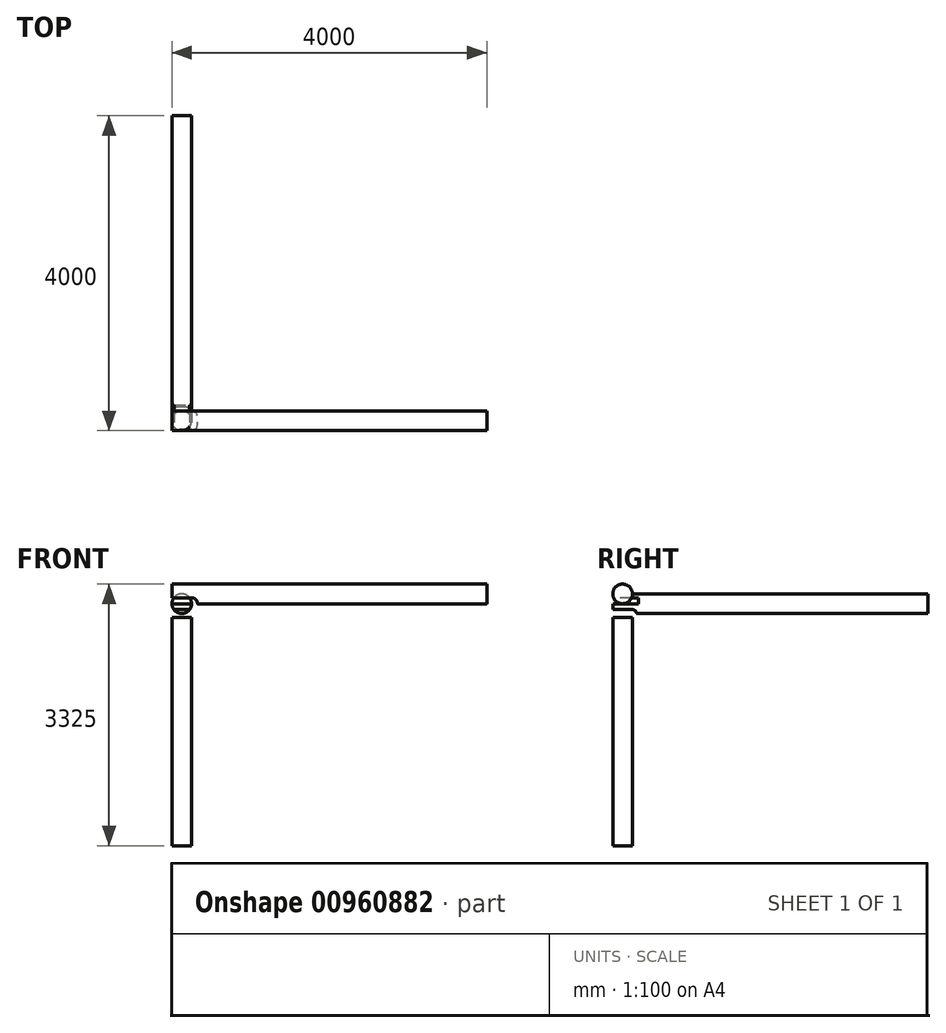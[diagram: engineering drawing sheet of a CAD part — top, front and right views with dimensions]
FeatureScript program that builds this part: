
annotation { "Feature Type Name" : "Feature", "Feature Type Description" : "" }
export const myFeature = defineFeature(function(context is Context, id is Id, definition is map)
    precondition{}
    {
        {
            var Q0;
            Q0=qCreatedBy(makeId("Top.planeOp"),FACE);
            var sketch = newSketch(context, id + "F0", { "sketchPlane" : qUnion([Q0])});
            skCircle(sketch, "E0", {"center": v(0, 0) * mm, "radius": 125 * mm});
            skSolve(sketch);
        }
        {
            var Q0;
            Q0=makeQuery(id+"F0.imprint","IMPRINT",FACE,{"disambiguationData":[TD([[makeQuery(id+"F0.imprint","IMPRINT",EDGE,{"derivedFrom":sQuery(id+"F0.wireOp",EDGE,"E0")}),1.0]])]});
            extrude(context, id + "F1", {"entities" : qUnion([Q0]), "oppositeDirection" : true, "depth" : 3000 * mm, "offsetDistance" : 25 * mm});
        }
        {
            var Q0;
            Q0=qCreatedBy(makeId("Front.planeOp"),FACE);
            cPlane(context, id + "F2", {"entities" : qUnion([Q0]), "cplaneType" : CPlaneType.OFFSET, "offset" : 125 * mm, "width" : 150 * mm, "height" : 150 * mm});
        }
        {
            var Q0;
            Q0=qCreatedBy(id+"F2.planeOp",FACE);
            var sketch = newSketch(context, id + "F3", { "sketchPlane" : qUnion([Q0])});
            skCircle(sketch, "E1", {"center": v(0, 75) * mm, "radius": 125 * mm});
            skSolve(sketch);
        }
        {
            var Q0;
            Q0=makeQuery(id+"F3.imprint","IMPRINT",FACE,{"disambiguationData":[TD([[makeQuery(id+"F3.imprint","IMPRINT",EDGE,{"derivedFrom":sQuery(id+"F3.wireOp",EDGE,"E1")}),1.0]])]});
            extrude(context, id + "F4", {"entities" : qUnion([Q0]), "oppositeDirection" : true, "depth" : 4000 * mm, "offsetDistance" : 25 * mm});
        }
        {
            var Q0;
            Q0=qCreatedBy(makeId("Right.planeOp"),FACE);
            var sketch = newSketch(context, id + "F5", { "sketchPlane" : qUnion([Q0])});
            skLineSegment(sketch, "E2", {"start": v(3875, -50) * mm, "end": v(-125, -50) * mm, "construction": true});
            skLineSegment(sketch, "E3", {"start": v(125, 0) * mm, "end": v(125, -3000) * mm, "construction": true});
            skLineSegment(sketch, "E4.0", {"start": v(-125, -50) * mm, "end": v(-125, 200) * mm, "construction": true});
            skLineSegment(sketch, "E5", {"start": v(125, 0) * mm, "end": v(-125, 0) * mm});
            skLineSegment(sketch, "E6", {"start": v(-125, 0) * mm, "end": v(-125, 150) * mm});
            skLineSegment(sketch, "E7", {"start": v(-125, 150) * mm, "end": v(125, 150) * mm});
            skLineSegment(sketch, "E8", {"start": v(125, 150) * mm, "end": v(125, 250) * mm});
            skLineSegment(sketch, "E9", {"start": v(125, 250) * mm, "end": v(-212.51, 250) * mm});
            skLineSegment(sketch, "E10", {"start": v(-212.51, 250) * mm, "end": v(-212.51, -100) * mm});
            skLineSegment(sketch, "E11", {"start": v(-212.51, -100) * mm, "end": v(216.52, -100) * mm});
            skLineSegment(sketch, "E12", {"start": v(216.52, -100) * mm, "end": v(216.52, -50) * mm});
            skLineSegment(sketch, "E13", {"start": v(-125, 200) * mm, "end": v(3875, 200) * mm, "construction": true});
            skArc(sketch, "E14", {"start": v(125, 0) * mm, "mid": v(160.36, -14.64) * mm, "end": v(175, -50) * mm});
            skLineSegment(sketch, "E15", {"start": v(175, -50) * mm, "end": v(216.52, -50) * mm});
            skSolve(sketch);
        }
        {
            var Q0;
            Q0=makeQuery(id+"F5.imprint","IMPRINT",FACE,{"disambiguationData":[TD([[makeQuery(id+"F5.imprint","IMPRINT",EDGE,{"derivedFrom":sQuery(id+"F5.wireOp",EDGE,"E5")}),1.0]])]});
            extrude(context, id + "F6", {"entities" : qUnion([Q0]), "operationType" : NewBodyOperationType.REMOVE, "endBound" : BoundingType.SYMMETRIC, "depth" : 400 * mm, "offsetDistance" : 25 * mm});
        }
        {
            var Q0;
            Q0=qCreatedBy(makeId("Right.planeOp"),FACE);
            cPlane(context, id + "F7", {"entities" : qUnion([Q0]), "cplaneType" : CPlaneType.OFFSET, "offset" : 125 * mm, "oppositeDirection" : true, "width" : 150 * mm, "height" : 150 * mm});
        }
        {
            var Q0;
            Q0=qCreatedBy(id+"F7.planeOp",FACE);
            var sketch = newSketch(context, id + "F8", { "sketchPlane" : qUnion([Q0])});
            skCircle(sketch, "E16", {"center": v(0, 200) * mm, "radius": 125 * mm});
            skSolve(sketch);
        }
        {
            var Q0;
            Q0=makeQuery(id+"F8.imprint","IMPRINT",FACE,{"disambiguationData":[TD([[makeQuery(id+"F8.imprint","IMPRINT",EDGE,{"derivedFrom":sQuery(id+"F8.wireOp",EDGE,"E16")}),1.0]])]});
            extrude(context, id + "F9", {"entities" : qUnion([Q0]), "depth" : 4000 * mm, "offsetDistance" : 25 * mm});
        }
        {
            var Q0;
            Q0=qCreatedBy(makeId("Front.planeOp"),FACE);
            var sketch = newSketch(context, id + "F10", { "sketchPlane" : qUnion([Q0])});
            skLineSegment(sketch, "E17.0", {"start": v(100, 150) * mm, "end": v(-100, 150) * mm, "construction": true});
            skLineSegment(sketch, "E18.0", {"start": v(-125, 325) * mm, "end": v(-125, 75) * mm, "construction": true});
            skLineSegment(sketch, "E19", {"start": v(3875, 75) * mm, "end": v(-125, 75) * mm, "construction": true});
            skArc(sketch, "E20.0.0", {"start": v(100, 0) * mm, "mid": v(125, 75) * mm, "end": v(100, 150) * mm, "construction": true});
            skArc(sketch, "E20.0.2", {"start": v(-100, 150) * mm, "mid": v(-125, 75) * mm, "end": v(-100, 0) * mm, "construction": true});
            skLineSegment(sketch, "E20.0.3", {"start": v(-100, 0) * mm, "end": v(100, 0) * mm, "construction": true});
            skLineSegment(sketch, "E21", {"start": v(-125, 150) * mm, "end": v(125, 150) * mm});
            skArc(sketch, "E22", {"start": v(125, 150) * mm, "mid": v(178.03, 128.03) * mm, "end": v(200, 75) * mm});
            skLineSegment(sketch, "E23", {"start": v(200, 75) * mm, "end": v(-125, 75) * mm});
            skLineSegment(sketch, "E24", {"start": v(-125, 150) * mm, "end": v(-125, 75) * mm});
            skSolve(sketch);
        }
        {
            var Q0;
            Q0 = qSketchRegion(id + "F10", true);
            extrude(context, id + "F11", {"entities" : qUnion([Q0]), "operationType" : NewBodyOperationType.REMOVE, "endBound" : BoundingType.SYMMETRIC, "oppositeDirection" : true, "depth" : 400 * mm, "offsetDistance" : 25 * mm});
        }
    });
